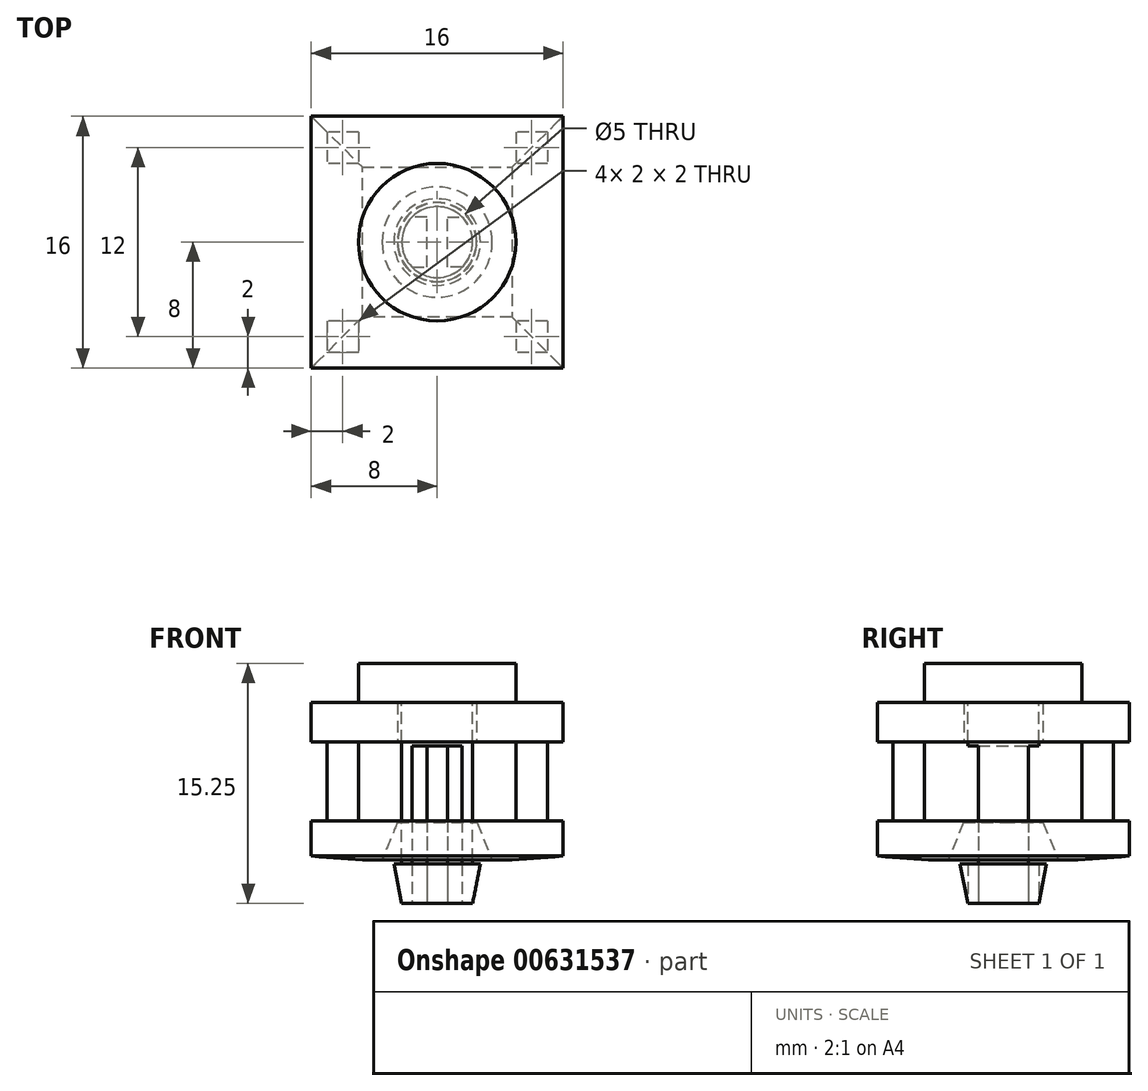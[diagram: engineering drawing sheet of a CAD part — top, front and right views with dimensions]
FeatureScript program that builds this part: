
annotation { "Feature Type Name" : "Feature", "Feature Type Description" : "" }
export const myFeature = defineFeature(function(context is Context, id is Id, definition is map)
    precondition{}
    {
        {
            assignVariable(context, id + "F0", {"name" : "PZ1", "anyValue" : 5});
        }
        {
            assignVariable(context, id + "F1", {"name" : "C1", "anyValue" : 0.25});
        }
        {
            var Q0;
            Q0=qCreatedBy(makeId("Top.planeOp"),FACE);
            cPlane(context, id + "F2", {"entities" : qUnion([Q0]), "cplaneType" : CPlaneType.OFFSET, "offset" : (getVariable(context, 'PZ1') / 2) * mm, "width" : 150 * mm, "height" : 150 * mm});
        }
        {
            var Q0;
            Q0=qCreatedBy(id+"F2.planeOp",FACE);
            var sketch = newSketch(context, id + "F3", { "sketchPlane" : qUnion([Q0])});
            skPoint(sketch, "E0.0", {"position": v(0, 0) * mm});
            skLineSegment(sketch, "E1.bottom", {"start": v(-8, -8) * mm, "end": v(8, -8) * mm});
            skLineSegment(sketch, "E1.top", {"start": v(-8, 8) * mm, "end": v(8, 8) * mm});
            skLineSegment(sketch, "E1.left", {"start": v(-8, -8) * mm, "end": v(-8, 8) * mm});
            skLineSegment(sketch, "E1.right", {"start": v(8, -8) * mm, "end": v(8, 8) * mm});
            skLineSegment(sketch, "E2.bottom", {"start": v(-5, -5) * mm, "end": v(-7, -5) * mm});
            skLineSegment(sketch, "E2.top", {"start": v(-5, -7) * mm, "end": v(-7, -7) * mm});
            skLineSegment(sketch, "E2.left", {"start": v(-5, -5) * mm, "end": v(-5, -7) * mm});
            skLineSegment(sketch, "E2.right", {"start": v(-7, -5) * mm, "end": v(-7, -7) * mm});
            skPoint(sketch, "E2.middle", {"position": v(-6, -6) * mm});
            skCircle(sketch, "E3", {"center": v(0, 0) * mm, "radius": 2.5 * mm});
            skPoint(sketch, "E4.0.1.0", {"position": v(-6, 6) * mm});
            skLineSegment(sketch, "E4.0.1.1", {"start": v(-5, 7) * mm, "end": v(-5, 5) * mm});
            skLineSegment(sketch, "E4.0.1.2", {"start": v(-5, 5) * mm, "end": v(-7, 5) * mm});
            skLineSegment(sketch, "E4.0.1.3", {"start": v(-5, 7) * mm, "end": v(-7, 7) * mm});
            skLineSegment(sketch, "E4.0.1.4", {"start": v(-7, 7) * mm, "end": v(-7, 5) * mm});
            skPoint(sketch, "E4.1.0.0", {"position": v(6, -6) * mm});
            skLineSegment(sketch, "E4.1.0.1", {"start": v(7, -5) * mm, "end": v(7, -7) * mm});
            skLineSegment(sketch, "E4.1.0.2", {"start": v(7, -7) * mm, "end": v(5, -7) * mm});
            skLineSegment(sketch, "E4.1.0.3", {"start": v(7, -5) * mm, "end": v(5, -5) * mm});
            skLineSegment(sketch, "E4.1.0.4", {"start": v(5, -5) * mm, "end": v(5, -7) * mm});
            skPoint(sketch, "E4.1.1.0", {"position": v(6, 6) * mm});
            skLineSegment(sketch, "E4.1.1.1", {"start": v(7, 7) * mm, "end": v(7, 5) * mm});
            skLineSegment(sketch, "E4.1.1.2", {"start": v(7, 5) * mm, "end": v(5, 5) * mm});
            skLineSegment(sketch, "E4.1.1.3", {"start": v(7, 7) * mm, "end": v(5, 7) * mm});
            skLineSegment(sketch, "E4.1.1.4", {"start": v(5, 7) * mm, "end": v(5, 5) * mm});
            skLineSegment(sketch, "E4.direction1", {"start": v(-7, -7) * mm, "end": v(5, -7) * mm, "construction": true});
            skLineSegment(sketch, "E4.direction2", {"start": v(-7, -7) * mm, "end": v(-7, 5) * mm, "construction": true});
            skSolve(sketch);
        }
        {
            var Q0;
            Q0=makeQuery(id+"F3.imprint","IMPRINT",FACE,{"disambiguationData":[TD([[makeQuery(id+"F3.imprint","IMPRINT",EDGE,{"derivedFrom":sQuery(id+"F3.wireOp",EDGE,"E1.bottom")}),1.0]])]});
            extrude(context, id + "F4", {"entities" : qUnion([Q0]), "depth" : (getVariable(context, 'PZ1') / 2) * mm, "offsetDistance" : 25 * mm});
        }
        {
            var Q0;
            Q0=makeQuery(id+"F4.opExtrude","SWEPT_BODY",BODY,{"disambiguationData":[OSD([sQuery(id+"F3.wireOp",EDGE,"E1.bottom"),sQuery(id+"F3.wireOp",EDGE,"E1.top"),sQuery(id+"F3.wireOp",EDGE,"E1.left"),sQuery(id+"F3.wireOp",EDGE,"E1.right"),sQuery(id+"F3.wireOp",EDGE,"E2.bottom"),sQuery(id+"F3.wireOp",EDGE,"E2.top"),sQuery(id+"F3.wireOp",EDGE,"E2.left"),sQuery(id+"F3.wireOp",EDGE,"E2.right"),sQuery(id+"F3.wireOp",EDGE,"E3"),sQuery(id+"F3.wireOp",EDGE,"E4.0.1.1"),sQuery(id+"F3.wireOp",EDGE,"E4.0.1.2"),sQuery(id+"F3.wireOp",EDGE,"E4.0.1.3"),sQuery(id+"F3.wireOp",EDGE,"E4.0.1.4"),sQuery(id+"F3.wireOp",EDGE,"E4.1.0.1"),sQuery(id+"F3.wireOp",EDGE,"E4.1.0.2"),sQuery(id+"F3.wireOp",EDGE,"E4.1.0.3"),sQuery(id+"F3.wireOp",EDGE,"E4.1.0.4"),sQuery(id+"F3.wireOp",EDGE,"E4.1.1.1"),sQuery(id+"F3.wireOp",EDGE,"E4.1.1.2"),sQuery(id+"F3.wireOp",EDGE,"E4.1.1.3"),sQuery(id+"F3.wireOp",EDGE,"E4.1.1.4")])]});
            transform(context, id + "F5", {"entities" : qUnion([Q0]), "transformType" : TransformType.TRANSLATION_3D, "dx" : 0 * mm, "dy" : 0 * mm, "dz" : (-1.5 * getVariable(context, 'PZ1')) * mm, "makeCopy" : true});
        }
        {
            var Q0;
            Q0=makeQuery(id+"F4.opExtrude","CAP_FACE",FACE,{"disambiguationData":[OSD([sQuery(id+"F3.wireOp",EDGE,"E1.bottom"),sQuery(id+"F3.wireOp",EDGE,"E1.top"),sQuery(id+"F3.wireOp",EDGE,"E1.left"),sQuery(id+"F3.wireOp",EDGE,"E1.right"),sQuery(id+"F3.wireOp",EDGE,"E2.bottom"),sQuery(id+"F3.wireOp",EDGE,"E2.top"),sQuery(id+"F3.wireOp",EDGE,"E2.left"),sQuery(id+"F3.wireOp",EDGE,"E2.right"),sQuery(id+"F3.wireOp",EDGE,"E3"),sQuery(id+"F3.wireOp",EDGE,"E4.0.1.1"),sQuery(id+"F3.wireOp",EDGE,"E4.0.1.2"),sQuery(id+"F3.wireOp",EDGE,"E4.0.1.3"),sQuery(id+"F3.wireOp",EDGE,"E4.0.1.4"),sQuery(id+"F3.wireOp",EDGE,"E4.1.0.1"),sQuery(id+"F3.wireOp",EDGE,"E4.1.0.2"),sQuery(id+"F3.wireOp",EDGE,"E4.1.0.3"),sQuery(id+"F3.wireOp",EDGE,"E4.1.0.4"),sQuery(id+"F3.wireOp",EDGE,"E4.1.1.1"),sQuery(id+"F3.wireOp",EDGE,"E4.1.1.2"),sQuery(id+"F3.wireOp",EDGE,"E4.1.1.3"),sQuery(id+"F3.wireOp",EDGE,"E4.1.1.4")])],"isStart":false});
            var sketch = newSketch(context, id + "F6", { "sketchPlane" : qUnion([Q0])});
            skLineSegment(sketch, "E5.0", {"start": v(-5, -7) * mm, "end": v(-7, -7) * mm});
            skLineSegment(sketch, "E6.0", {"start": v(-7, -5) * mm, "end": v(-7, -7) * mm});
            skLineSegment(sketch, "E7.0", {"start": v(-5, -5) * mm, "end": v(-7, -5) * mm});
            skLineSegment(sketch, "E8.0", {"start": v(-5, -5) * mm, "end": v(-5, -7) * mm});
            skPoint(sketch, "E9.0", {"position": v(-6, -6) * mm});
            skLineSegment(sketch, "E10.0", {"start": v(-5, 5) * mm, "end": v(-7, 5) * mm});
            skLineSegment(sketch, "E11.0", {"start": v(-7, 7) * mm, "end": v(-7, 5) * mm});
            skLineSegment(sketch, "E12.0", {"start": v(-5, 7) * mm, "end": v(-7, 7) * mm});
            skLineSegment(sketch, "E13.0", {"start": v(-5, 7) * mm, "end": v(-5, 5) * mm});
            skPoint(sketch, "E14.0", {"position": v(-6, 6) * mm});
            skLineSegment(sketch, "E15.0", {"start": v(7, -7) * mm, "end": v(5, -7) * mm});
            skLineSegment(sketch, "E16.0", {"start": v(7, -5) * mm, "end": v(7, -7) * mm});
            skLineSegment(sketch, "E17.0", {"start": v(7, -5) * mm, "end": v(5, -5) * mm});
            skLineSegment(sketch, "E18.0", {"start": v(5, -5) * mm, "end": v(5, -7) * mm});
            skPoint(sketch, "E19.0", {"position": v(6, -6) * mm});
            skLineSegment(sketch, "E20.0", {"start": v(7, 5) * mm, "end": v(5, 5) * mm});
            skLineSegment(sketch, "E21.0", {"start": v(7, 7) * mm, "end": v(7, 5) * mm});
            skLineSegment(sketch, "E22.0", {"start": v(7, 7) * mm, "end": v(5, 7) * mm});
            skLineSegment(sketch, "E23.0", {"start": v(5, 7) * mm, "end": v(5, 5) * mm});
            skPoint(sketch, "E24.0", {"position": v(6, 6) * mm});
            skSolve(sketch);
        }
        {
            var Q0;
            Q0=makeQuery(id+"F6.imprint","IMPRINT",FACE,{"disambiguationData":[TD([[makeQuery(id+"F6.imprint","IMPRINT",EDGE,{"derivedFrom":sQuery(id+"F6.wireOp",EDGE,"E5.0")}),-1.0]])]});
            var Q1;
            Q1=makeQuery(id+"F6.imprint","IMPRINT",FACE,{"disambiguationData":[TD([[makeQuery(id+"F6.imprint","IMPRINT",EDGE,{"derivedFrom":sQuery(id+"F6.wireOp",EDGE,"E10.0")}),-1.0]])]});
            var Q2;
            Q2=makeQuery(id+"F6.imprint","IMPRINT",FACE,{"disambiguationData":[TD([[makeQuery(id+"F6.imprint","IMPRINT",EDGE,{"derivedFrom":sQuery(id+"F6.wireOp",EDGE,"E20.0")}),-1.0]])]});
            var Q3;
            Q3=makeQuery(id+"F6.imprint","IMPRINT",FACE,{"disambiguationData":[TD([[makeQuery(id+"F6.imprint","IMPRINT",EDGE,{"derivedFrom":sQuery(id+"F6.wireOp",EDGE,"E15.0")}),-1.0]])]});
            extrude(context, id + "F7", {"entities" : qUnion([Q0, Q1, Q2, Q3]), "operationType" : NewBodyOperationType.ADD, "oppositeDirection" : true, "depth" : 2 * getVariable(context, 'PZ1') * mm, "offsetDistance" : 25 * mm});
        }
        {
            var Q0;
            Q0=qCreatedBy(makeId("Front.planeOp"),FACE);
            var sketch = newSketch(context, id + "F8", { "sketchPlane" : qUnion([Q0])});
            skLineSegment(sketch, "E25", {"start": v(0, 8.34) * mm, "end": v(0, -8.43) * mm, "construction": true});
            skLineSegment(sketch, "E26", {"start": v(0, 7.5) * mm, "end": v(-5, 7.5) * mm});
            skLineSegment(sketch, "E27", {"start": v(-5, 7.5) * mm, "end": v(-5, 5) * mm});
            skLineSegment(sketch, "E28", {"start": v(-5, 5) * mm, "end": v(-2.25, 5) * mm});
            skLineSegment(sketch, "E29", {"start": v(-2.25, 5) * mm, "end": v(-2.25, -5.25) * mm});
            skLineSegment(sketch, "E30", {"start": v(-2.25, -5.25) * mm, "end": v(-2.75, -5.25) * mm});
            skLineSegment(sketch, "E31", {"start": v(-2.75, -5.25) * mm, "end": v(-2.25, -7.75) * mm});
            skLineSegment(sketch, "E32", {"start": v(-2.25, -7.75) * mm, "end": v(0, -7.75) * mm});
            skLineSegment(sketch, "E33", {"start": v(0, -7.75) * mm, "end": v(0, 7.5) * mm});
            skLineSegment(sketch, "E34.0", {"start": v(-2.5, 5) * mm, "end": v(2.5, 5) * mm, "construction": true});
            skLineSegment(sketch, "E35.0", {"start": v(-2.5, -5) * mm, "end": v(2.5, -5) * mm, "construction": true});
            skSolve(sketch);
        }
        {
            var Q0;
            Q0=makeQuery(id+"F8.imprint","IMPRINT",FACE,{"disambiguationData":[TD([[makeQuery(id+"F8.imprint","IMPRINT",EDGE,{"derivedFrom":sQuery(id+"F8.wireOp",EDGE,"E26")}),1.0]])]});
            var Q1;
            Q1=sQuery(id+"F8.wireOp",EDGE,"E25");
            revolve(context, id + "F9", {"entities" : qUnion([Q0]), "axis" : qUnion([Q1]), "revolveType" : RevolveType.FULL});
        }
        {
            var Q0;
            Q0=makeQuery(id+"F9.opRevolve","SWEPT_FACE",FACE,{"disambiguationData":[OSD([sQuery(id+"F8.wireOp",EDGE,"E32")])]});
            var sketch = newSketch(context, id + "F10", { "sketchPlane" : qUnion([Q0])});
            skCircle(sketch, "E36.0", {"center": v(0, 0) * mm, "radius": 2.75 * mm});
            skCircle(sketch, "E37.0", {"center": v(0, 0) * mm, "radius": 2.25 * mm, "construction": true});
            skLineSegment(sketch, "E38.0", {"start": v(-2.5, 0) * mm, "end": v(2.5, 0) * mm, "construction": true});
            skCircle(sketch, "E39.0", {"center": v(0, 0) * mm, "radius": 2.5 * mm, "construction": true});
            skCircle(sketch, "E40.0", {"center": v(0.65, 0) * mm, "radius": 2.75 * mm, "construction": true});
            skLineSegment(sketch, "E41", {"start": v(-3.74, -3.74) * mm, "end": v(3.92, 3.92) * mm, "construction": true});
            skPoint(sketch, "E42", {"position": v(-1.6, -1.6) * mm});
            skLineSegment(sketch, "E43.bottom", {"start": v(-1.6, -1.6) * mm, "end": v(1.6, -1.6) * mm, "construction": true});
            skLineSegment(sketch, "E43.top", {"start": v(-1.6, 1.6) * mm, "end": v(1.6, 1.6) * mm, "construction": true});
            skLineSegment(sketch, "E43.left", {"start": v(-1.6, -1.6) * mm, "end": v(-1.6, 1.6) * mm, "construction": true});
            skLineSegment(sketch, "E43.right", {"start": v(1.6, -1.6) * mm, "end": v(1.6, 1.6) * mm, "construction": true});
            skLineSegment(sketch, "E44", {"start": v(0, -3.66) * mm, "end": v(0, 3.9) * mm, "construction": true});
            skLineSegment(sketch, "E45", {"start": v(-2.24, 1.6) * mm, "end": v(-0.65, 1.6) * mm});
            skLineSegment(sketch, "E46", {"start": v(-0.65, 1.6) * mm, "end": v(-0.65, -1.6) * mm});
            skLineSegment(sketch, "E47", {"start": v(-0.65, -1.6) * mm, "end": v(-2.24, -1.6) * mm});
            skLineSegment(sketch, "E48.MirrorCS", {"start": v(0.65, -1.6) * mm, "end": v(2.24, -1.6) * mm});
            skLineSegment(sketch, "E49.MirrorCS", {"start": v(0.65, 1.6) * mm, "end": v(0.65, -1.6) * mm});
            skLineSegment(sketch, "E50.MirrorCS", {"start": v(2.24, 1.6) * mm, "end": v(0.65, 1.6) * mm});
            skSolve(sketch);
        }
        {
            var Q0;
            {var subQ0=sQuery(id+"F10.wireOp",EDGE,"E45");var subQ1=sQuery(id+"F10.wireOp",EDGE,"E36.0");var subQ2=makeQuery(id+"F10.imprint","INTERSECT",VERTEX,{"derivedFrom":[subQ1,subQ0]});Q0=makeQuery(id+"F10.imprint","IMPRINT",FACE,{"disambiguationData":[TD([[makeQuery(id+"F10.imprint","IMPRINT",EDGE,{"disambiguationData":[TD([[subQ2,-1.0]])],"derivedFrom":subQ1}),-1.0]])]});}
            var Q1;
            {var subQ5=sQuery(id+"F10.wireOp",EDGE,"E46");Q1=makeQuery(id+"F10.imprint","IMPRINT",FACE,{"disambiguationData":[TD([[makeQuery(id+"F10.imprint","IMPRINT",EDGE,{"derivedFrom":subQ5}),1.0]])]});}
            var Q2;
            {var subQ0=sQuery(id+"F10.wireOp",EDGE,"E47");var subQ1=sQuery(id+"F10.wireOp",EDGE,"E36.0");var subQ2=makeQuery(id+"F10.imprint","INTERSECT",VERTEX,{"derivedFrom":[subQ1,subQ0]});Q2=makeQuery(id+"F10.imprint","IMPRINT",FACE,{"disambiguationData":[TD([[makeQuery(id+"F10.imprint","IMPRINT",EDGE,{"disambiguationData":[TD([[subQ2,1.0]])],"derivedFrom":subQ1}),-1.0]])]});}
            extrude(context, id + "F11", {"entities" : qUnion([Q0, Q1, Q2]), "operationType" : NewBodyOperationType.REMOVE, "oppositeDirection" : true, "depth" : 10 * mm, "offsetDistance" : 25 * mm});
        }
        {
            var Q0;
            Q0=makeQuery(id+"F7.opExtrude","CAP_FACE",FACE,{"disambiguationData":[OSD([sQuery(id+"F6.wireOp",EDGE,"E15.0"),sQuery(id+"F6.wireOp",EDGE,"E16.0"),sQuery(id+"F6.wireOp",EDGE,"E17.0"),sQuery(id+"F6.wireOp",EDGE,"E18.0")])],"isStart":false});
            chamfer(context, id + "F12", {"entities" : qUnion([Q0]), "chamferType" : ChamferType.TWO_OFFSETS, "width1" : (getVariable(context, 'C1')) * mm, "oppositeDirection" : false, "width2" : (getVariable(context, 'PZ1') / 2) * mm});
        }
        {
            var Q0;
            Q0=makeQuery(id+"F7.opExtrude","CAP_FACE",FACE,{"disambiguationData":[OSD([sQuery(id+"F6.wireOp",EDGE,"E20.0"),sQuery(id+"F6.wireOp",EDGE,"E21.0"),sQuery(id+"F6.wireOp",EDGE,"E22.0"),sQuery(id+"F6.wireOp",EDGE,"E23.0")])],"isStart":false});
            chamfer(context, id + "F13", {"entities" : qUnion([Q0]), "chamferType" : ChamferType.TWO_OFFSETS, "width1" : (getVariable(context, 'C1')) * mm, "oppositeDirection" : false, "width2" : (getVariable(context, 'PZ1') / 2) * mm});
        }
        {
            var Q0;
            Q0=makeQuery(id+"F7.opExtrude","CAP_FACE",FACE,{"disambiguationData":[OSD([sQuery(id+"F6.wireOp",EDGE,"E10.0"),sQuery(id+"F6.wireOp",EDGE,"E11.0"),sQuery(id+"F6.wireOp",EDGE,"E12.0"),sQuery(id+"F6.wireOp",EDGE,"E13.0")])],"isStart":false});
            chamfer(context, id + "F14", {"entities" : qUnion([Q0]), "chamferType" : ChamferType.TWO_OFFSETS, "width1" : 0.25 * mm, "oppositeDirection" : false, "width2" : (getVariable(context, 'PZ1') / 2) * mm});
        }
        {
            var Q0;
            Q0=makeQuery(id+"F7.opExtrude","CAP_FACE",FACE,{"disambiguationData":[OSD([sQuery(id+"F6.wireOp",EDGE,"E5.0"),sQuery(id+"F6.wireOp",EDGE,"E6.0"),sQuery(id+"F6.wireOp",EDGE,"E7.0"),sQuery(id+"F6.wireOp",EDGE,"E8.0")])],"isStart":false});
            chamfer(context, id + "F15", {"entities" : qUnion([Q0]), "chamferType" : ChamferType.TWO_OFFSETS, "width1" : (getVariable(context, 'C1')) * mm, "oppositeDirection" : false, "width2" : (getVariable(context, 'PZ1') / 2) * mm, "tangentPropagation" : true});
        }
    });
